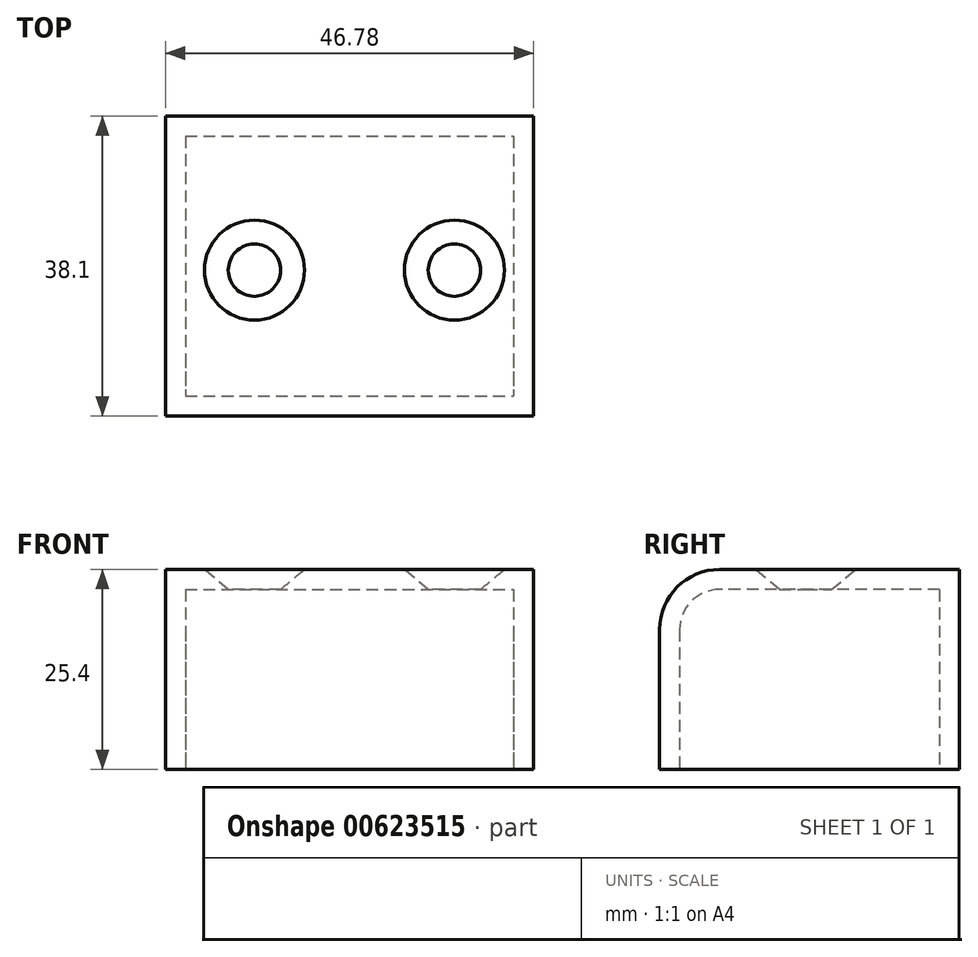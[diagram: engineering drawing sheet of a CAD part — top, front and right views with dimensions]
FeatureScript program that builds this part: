
annotation { "Feature Type Name" : "Feature", "Feature Type Description" : "" }
export const myFeature = defineFeature(function(context is Context, id is Id, definition is map)
    precondition{}
    {
        {
            var Q0;
            Q0=qCreatedBy(makeId("Top.planeOp"),FACE);
            var sketch = newSketch(context, id + "F0", { "sketchPlane" : qUnion([Q0])});
            skLineSegment(sketch, "E0.bottom", {"start": v(-24.01, 19.57) * mm, "end": v(22.77, 19.57) * mm});
            skLineSegment(sketch, "E0.top", {"start": v(-24.01, -18.53) * mm, "end": v(22.77, -18.53) * mm});
            skLineSegment(sketch, "E0.left", {"start": v(-24.01, 19.57) * mm, "end": v(-24.01, -18.53) * mm});
            skLineSegment(sketch, "E0.right", {"start": v(22.77, 19.57) * mm, "end": v(22.77, -18.53) * mm});
            skSolve(sketch);
        }
        {
            var Q0;
            Q0=makeQuery(id+"F0.imprint","IMPRINT",FACE,{"disambiguationData":[TD([[makeQuery(id+"F0.imprint","IMPRINT",EDGE,{"derivedFrom":sQuery(id+"F0.wireOp",EDGE,"E0.bottom")}),-1.0]])]});
            extrude(context, id + "F1", {"entities" : qUnion([Q0]), "depth" : 25.4 * mm, "offsetDistance" : 25.4 * mm});
        }
        {
            var Q0;
            Q0=makeQuery(id+"F1.opExtrude","CAP_EDGE",EDGE,{"disambiguationData":[OSD([sQuery(id+"F0.wireOp",EDGE,"E0.top")])],"isStart":false});
            fillet(context, id + "F2", {"entities" : qUnion([Q0]), "radius" : 7.62 * mm, "tangentPropagation" : true, "allowEdgeOverflow" : false});
        }
        {
            var Q0;
            Q0=makeQuery(id+"F1.opExtrude","CAP_FACE",FACE,{"disambiguationData":[OSD([sQuery(id+"F0.wireOp",EDGE,"E0.bottom"),sQuery(id+"F0.wireOp",EDGE,"E0.top"),sQuery(id+"F0.wireOp",EDGE,"E0.left"),sQuery(id+"F0.wireOp",EDGE,"E0.right")])],"isStart":true});
            shell(context, id + "F3", {"entities" : qUnion([Q0]), "thickness" : 2.54 * mm});
        }
        {
            var Q0;
            Q0=makeQuery(id+"F1.opExtrude","CAP_FACE",FACE,{"disambiguationData":[OSD([sQuery(id+"F0.wireOp",EDGE,"E0.bottom"),sQuery(id+"F0.wireOp",EDGE,"E0.top"),sQuery(id+"F0.wireOp",EDGE,"E0.left"),sQuery(id+"F0.wireOp",EDGE,"E0.right")])],"isStart":false});
            var sketch = newSketch(context, id + "F4", { "sketchPlane" : qUnion([Q0])});
            skPoint(sketch, "E1", {"position": v(-12.7, 0) * mm});
            skPoint(sketch, "E2", {"position": v(12.7, 0) * mm});
            skSolve(sketch);
        }
        {
            var Q0;
            Q0=sQuery(id+"F4.wireOp",VERTEX,"E1");
            var Q1;
            Q1=sQuery(id+"F4.wireOp",VERTEX,"E2");
            var Q2;
            Q2=makeQuery(id+"F1.opExtrude","SWEPT_BODY",BODY,{"disambiguationData":[OSD([sQuery(id+"F0.wireOp",EDGE,"E0.bottom"),sQuery(id+"F0.wireOp",EDGE,"E0.top"),sQuery(id+"F0.wireOp",EDGE,"E0.left"),sQuery(id+"F0.wireOp",EDGE,"E0.right")])]});
            hole(context, id + "F5", {"style" : HoleStyle.C_SINK, "endStyle" : HoleEndStyle.THROUGH, "holeDiameter" : 6.35 * mm, "cSinkDiameter" : 12.7 * mm, "cSinkAngle" : 100 * degree, "majorDiameter" : 6.35 * mm, "isTappedThrough" : true, "tappedDepth" : 12.7 * mm, "tapClearance" : 3, "startFromSketch" : true, "locations" : qUnion([Q0, Q1]), "scope" : qUnion([Q2])});
        }
    });
